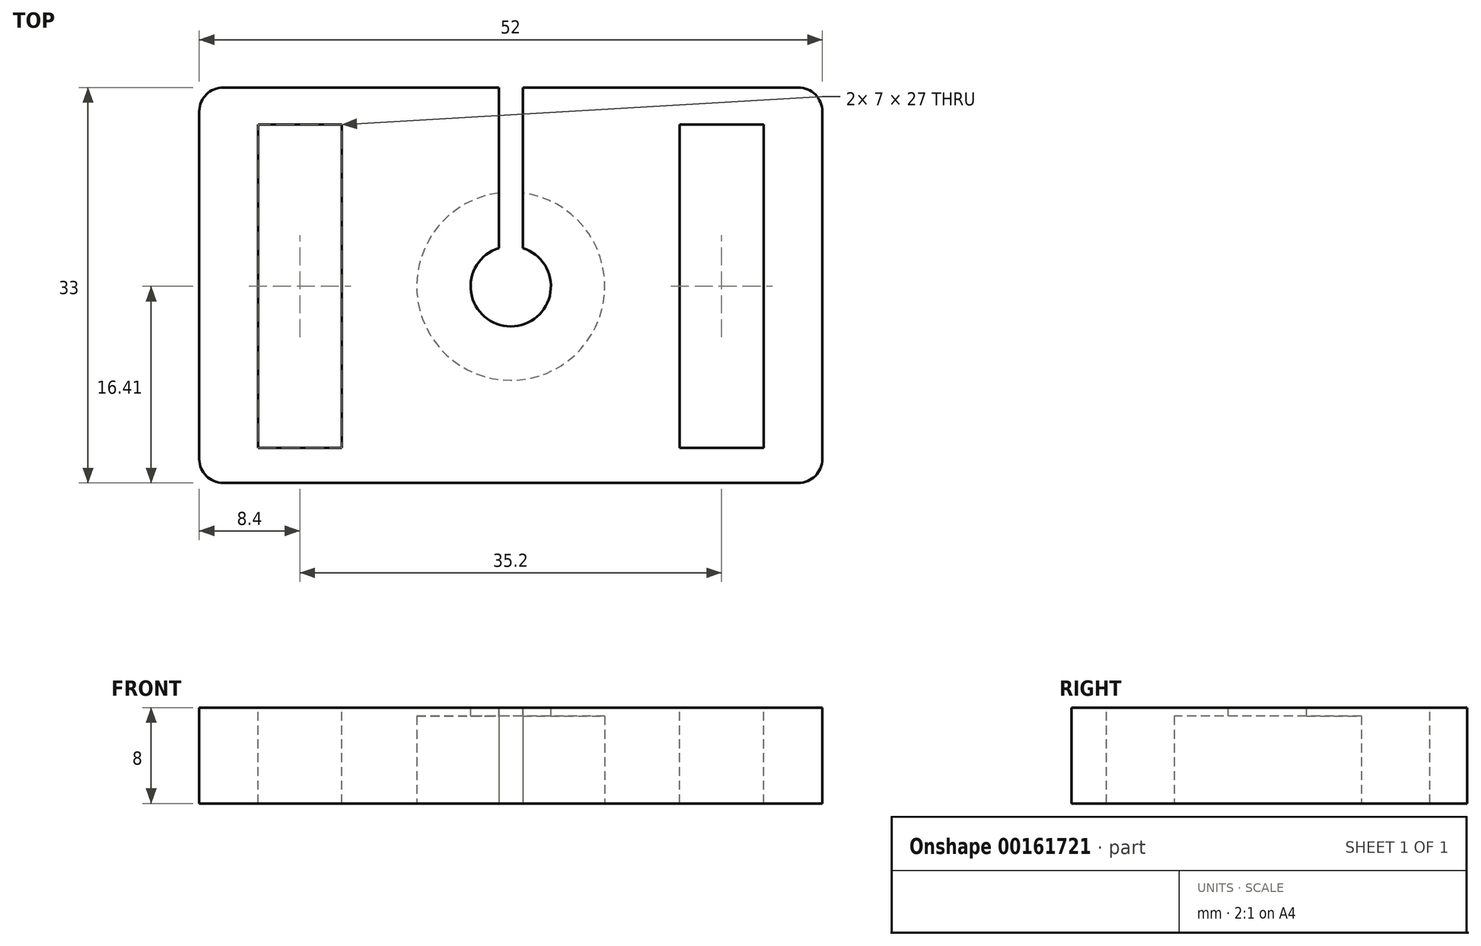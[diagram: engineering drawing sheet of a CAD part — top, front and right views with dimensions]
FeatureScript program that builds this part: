
annotation { "Feature Type Name" : "Feature", "Feature Type Description" : "" }
export const myFeature = defineFeature(function(context is Context, id is Id, definition is map)
    precondition{}
    {
        {
            var Q0;
            Q0=qCreatedBy(makeId("Top.planeOp"),FACE);
            var sketch = newSketch(context, id + "F0", { "sketchPlane" : qUnion([Q0])});
            skLineSegment(sketch, "E0.bottom", {"start": v(26, -16.41) * mm, "end": v(-26, -16.41) * mm});
            skLineSegment(sketch, "E0.top", {"start": v(26, 16.59) * mm, "end": v(-26, 16.59) * mm});
            skLineSegment(sketch, "E0.left", {"start": v(26, -16.41) * mm, "end": v(26, 16.59) * mm});
            skLineSegment(sketch, "E0.right", {"start": v(-26, -16.41) * mm, "end": v(-26, 16.59) * mm});
            skPoint(sketch, "E0.middle", {"position": v(0, 0.09) * mm});
            skSolve(sketch);
        }
        {
            var Q0;
            Q0=makeQuery(id+"F0.imprint","IMPRINT",FACE,{"disambiguationData":[TD([[makeQuery(id+"F0.imprint","IMPRINT",EDGE,{"derivedFrom":sQuery(id+"F0.wireOp",EDGE,"E0.bottom")}),-1.0]])]});
            extrude(context, id + "F1", {"entities" : qUnion([Q0]), "depth" : 8 * mm});
        }
        {
            var Q0;
            Q0=makeQuery(id+"F1.opExtrude","CAP_FACE",FACE,{"disambiguationData":[OSD([sQuery(id+"F0.wireOp",EDGE,"E0.bottom"),sQuery(id+"F0.wireOp",EDGE,"E0.top"),sQuery(id+"F0.wireOp",EDGE,"E0.left"),sQuery(id+"F0.wireOp",EDGE,"E0.right")])],"isStart":true});
            var sketch = newSketch(context, id + "F2", { "sketchPlane" : qUnion([Q0])});
            skCircle(sketch, "E1", {"center": v(0, 0) * mm, "radius": 7.85 * mm});
            skSolve(sketch);
        }
        {
            var Q0;
            Q0=makeQuery(id+"F2.imprint","IMPRINT",FACE,{"disambiguationData":[TD([[makeQuery(id+"F2.imprint","IMPRINT",EDGE,{"derivedFrom":sQuery(id+"F2.wireOp",EDGE,"E1")}),1.0]])]});
            extrude(context, id + "F3", {"entities" : qUnion([Q0]), "operationType" : NewBodyOperationType.REMOVE, "oppositeDirection" : true, "depth" : 7.3 * mm});
        }
        {
            var Q0;
            Q0=makeQuery(id+"F1.opExtrude","CAP_FACE",FACE,{"disambiguationData":[OSD([sQuery(id+"F0.wireOp",EDGE,"E0.bottom"),sQuery(id+"F0.wireOp",EDGE,"E0.top"),sQuery(id+"F0.wireOp",EDGE,"E0.left"),sQuery(id+"F0.wireOp",EDGE,"E0.right")])],"isStart":false});
            var sketch = newSketch(context, id + "F4", { "sketchPlane" : qUnion([Q0])});
            skCircle(sketch, "E2", {"center": v(0, 0) * mm, "radius": 3.35 * mm});
            skSolve(sketch);
        }
        {
            var Q0;
            Q0=makeQuery(id+"F4.imprint","IMPRINT",FACE,{"disambiguationData":[TD([[makeQuery(id+"F4.imprint","IMPRINT",EDGE,{"derivedFrom":sQuery(id+"F4.wireOp",EDGE,"E2")}),1.0]])]});
            extrude(context, id + "F5", {"entities" : qUnion([Q0]), "operationType" : NewBodyOperationType.REMOVE, "oppositeDirection" : true, "depth" : 10 * mm});
        }
        {
            var Q0;
            Q0=makeQuery(id+"F1.opExtrude","SWEPT_EDGE",EDGE,{"disambiguationData":[OSD([sQuery(id+"F0.wireOp",EDGE,"E0.bottom"),sQuery(id+"F0.wireOp",EDGE,"E0.left")])]});
            var Q1;
            Q1=makeQuery(id+"F1.opExtrude","SWEPT_EDGE",EDGE,{"disambiguationData":[OSD([sQuery(id+"F0.wireOp",EDGE,"E0.top"),sQuery(id+"F0.wireOp",EDGE,"E0.left")])]});
            var Q2;
            Q2=makeQuery(id+"F1.opExtrude","SWEPT_EDGE",EDGE,{"disambiguationData":[OSD([sQuery(id+"F0.wireOp",EDGE,"E0.top"),sQuery(id+"F0.wireOp",EDGE,"E0.right")])]});
            var Q3;
            Q3=makeQuery(id+"F1.opExtrude","SWEPT_EDGE",EDGE,{"disambiguationData":[OSD([sQuery(id+"F0.wireOp",EDGE,"E0.bottom"),sQuery(id+"F0.wireOp",EDGE,"E0.right")])]});
            fillet(context, id + "F6", {"entities" : qUnion([Q0, Q1, Q2, Q3]), "radius" : 2 * mm, "tangentPropagation" : true, "allowEdgeOverflow" : false});
        }
        {
            var Q0;
            Q0=qCreatedBy(makeId("Top.planeOp"),FACE);
            var sketch = newSketch(context, id + "F7", { "sketchPlane" : qUnion([Q0])});
            skLineSegment(sketch, "E3.bottom", {"start": v(-1, 0) * mm, "end": v(1, 0) * mm});
            skLineSegment(sketch, "E3.top", {"start": v(-1, 22.6) * mm, "end": v(1, 22.6) * mm});
            skLineSegment(sketch, "E3.left", {"start": v(-1, 0) * mm, "end": v(-1, 22.6) * mm});
            skLineSegment(sketch, "E3.right", {"start": v(1, 0) * mm, "end": v(1, 22.6) * mm});
            skSolve(sketch);
        }
        {
            var Q0;
            Q0=makeQuery(id+"F7.imprint","IMPRINT",FACE,{"disambiguationData":[TD([[makeQuery(id+"F7.imprint","IMPRINT",EDGE,{"derivedFrom":sQuery(id+"F7.wireOp",EDGE,"E3.bottom")}),1.0]])]});
            extrude(context, id + "F8", {"entities" : qUnion([Q0]), "operationType" : NewBodyOperationType.REMOVE, "depth" : 18 * mm});
        }
        {
            var Q0;
            Q0=makeQuery(id+"F1.opExtrude","CAP_FACE",FACE,{"disambiguationData":[OSD([sQuery(id+"F0.wireOp",EDGE,"E0.bottom"),sQuery(id+"F0.wireOp",EDGE,"E0.top"),sQuery(id+"F0.wireOp",EDGE,"E0.left"),sQuery(id+"F0.wireOp",EDGE,"E0.right")])],"isStart":false});
            var sketch = newSketch(context, id + "F9", { "sketchPlane" : qUnion([Q0])});
            skLineSegment(sketch, "E4.bottom", {"start": v(-14.1, -13.5) * mm, "end": v(-21.1, -13.5) * mm});
            skLineSegment(sketch, "E4.top", {"start": v(-14.1, 13.5) * mm, "end": v(-21.1, 13.5) * mm});
            skLineSegment(sketch, "E4.left", {"start": v(-14.1, -13.5) * mm, "end": v(-14.1, 13.5) * mm});
            skLineSegment(sketch, "E4.right", {"start": v(-21.1, -13.5) * mm, "end": v(-21.1, 13.5) * mm});
            skPoint(sketch, "E4.middle", {"position": v(-17.6, 0) * mm});
            skLineSegment(sketch, "E5", {"start": v(0, -24.75) * mm, "end": v(0, 29.85) * mm, "construction": true});
            skPoint(sketch, "E6.MirrorP", {"position": v(17.6, 0) * mm});
            skLineSegment(sketch, "E7.MirrorCS", {"start": v(14.1, -13.5) * mm, "end": v(21.1, -13.5) * mm});
            skLineSegment(sketch, "E8.MirrorCS", {"start": v(14.1, 13.5) * mm, "end": v(21.1, 13.5) * mm});
            skLineSegment(sketch, "E9.MirrorCS", {"start": v(14.1, -13.5) * mm, "end": v(14.1, 13.5) * mm});
            skLineSegment(sketch, "E10.MirrorCS", {"start": v(21.1, -13.5) * mm, "end": v(21.1, 13.5) * mm});
            skSolve(sketch);
        }
        {
            var Q0;
            Q0 = qSketchRegion(id + "F9", true);
            extrude(context, id + "F10", {"entities" : qUnion([Q0]), "operationType" : NewBodyOperationType.REMOVE, "endBound" : BoundingType.THROUGH_ALL, "oppositeDirection" : true, "depth" : 25 * mm});
        }
    });
